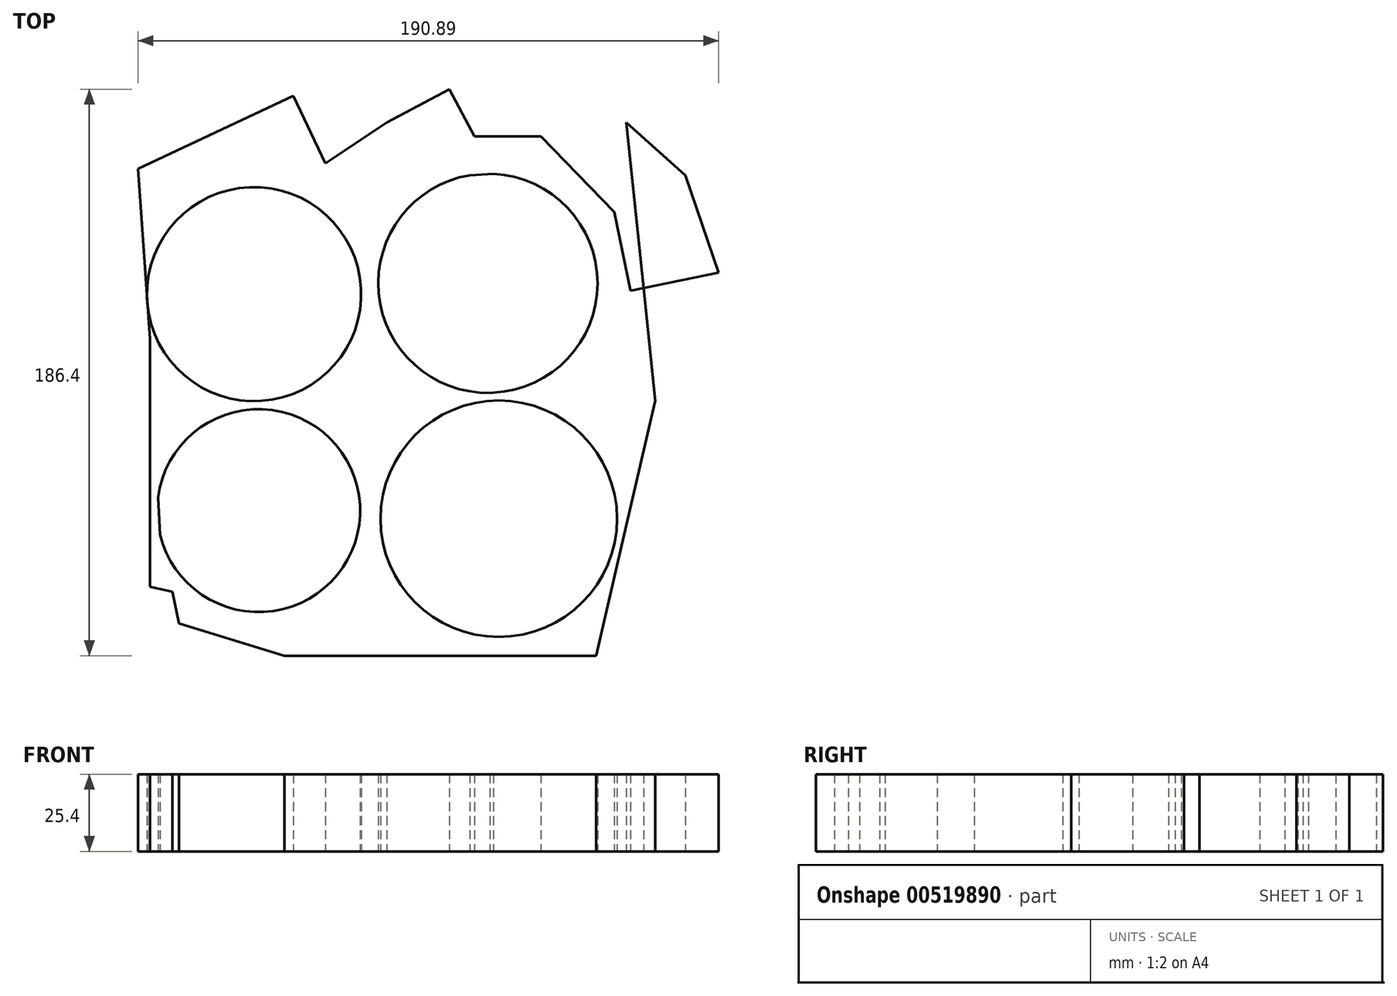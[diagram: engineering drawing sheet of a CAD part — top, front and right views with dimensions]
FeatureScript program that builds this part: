
annotation { "Feature Type Name" : "Feature", "Feature Type Description" : "" }
export const myFeature = defineFeature(function(context is Context, id is Id, definition is map)
    precondition{}
    {
        {
            var Q0;
            Q0=qCreatedBy(makeId("Top.planeOp"),FACE);
            var sketch = newSketch(context, id + "F0", { "sketchPlane" : qUnion([Q0])});
            skCircle(sketch, "E0", {"center": v(-41.12, 35.01) * mm, "radius": 35.2 * mm});
            skCircle(sketch, "E1", {"center": v(35.76, 38.59) * mm, "radius": 36.06 * mm});
            skCircle(sketch, "E2", {"center": v(-39.63, -36.2) * mm, "radius": 33.38 * mm});
            skCircle(sketch, "E3", {"center": v(39.33, -38.89) * mm, "radius": 38.9 * mm});
            skLineSegment(sketch, "E4", {"start": v(-39.94, 70.2) * mm, "end": v(37.6, 74.6) * mm});
            skLineSegment(sketch, "E5", {"start": v(37.6, 2.58) * mm, "end": v(-39.87, -0.17) * mm});
            skLineSegment(sketch, "E6", {"start": v(-39.87, -69.58) * mm, "end": v(37.6, -77.82) * mm});
            skLineSegment(sketch, "E7", {"start": v(-76.32, 34.14) * mm, "end": v(-72.07, -44.07) * mm});
            skLineSegment(sketch, "E8", {"start": v(71.81, 37.94) * mm, "end": v(77.5, -31.34) * mm});
            skSolve(sketch);
        }
        {
            var Q0;
            {var subQ0=sQuery(id+"F0.wireOp",EDGE,"E3");var subQ1=makeQuery(id+"F0.imprint","INTERSECT",VERTEX,{"derivedFrom":[subQ0,sQuery(id+"F0.wireOp",EDGE,"E8")]});Q0=makeQuery(id+"F0.imprint","IMPRINT",FACE,{"disambiguationData":[TD([[makeQuery(id+"F0.imprint","IMPRINT",EDGE,{"disambiguationData":[TD([[subQ1,-1.0]])],"derivedFrom":subQ0}),1.0]])]});}
            var Q1;
            {var subQ0=sQuery(id+"F0.wireOp",EDGE,"E2");var subQ1=makeQuery(id+"F0.imprint","INTERSECT",VERTEX,{"derivedFrom":[subQ0,sQuery(id+"F0.wireOp",EDGE,"E6")]});Q1=makeQuery(id+"F0.imprint","IMPRINT",FACE,{"disambiguationData":[TD([[makeQuery(id+"F0.imprint","IMPRINT",EDGE,{"disambiguationData":[TD([[subQ1,1.0]])],"derivedFrom":subQ0}),1.0]])]});}
            var Q2;
            {var subQ0=sQuery(id+"F0.wireOp",EDGE,"E0");var subQ1=makeQuery(id+"F0.imprint","INTERSECT",VERTEX,{"derivedFrom":[subQ0,sQuery(id+"F0.wireOp",EDGE,"E4")]});Q2=makeQuery(id+"F0.imprint","IMPRINT",FACE,{"disambiguationData":[TD([[makeQuery(id+"F0.imprint","IMPRINT",EDGE,{"disambiguationData":[TD([[subQ1,-1.0]])],"derivedFrom":subQ0}),1.0]])]});}
            var Q3;
            {var subQ0=sQuery(id+"F0.wireOp",EDGE,"E4");var subQ1=sQuery(id+"F0.wireOp",EDGE,"E1");var subQ6=makeQuery(id+"F0.imprint","INTERSECT",VERTEX,{"disambiguationData":[OD(1.0)],"derivedFrom":[subQ1,subQ0]});Q3=makeQuery(id+"F0.imprint","IMPRINT",FACE,{"disambiguationData":[TD([[makeQuery(id+"F0.imprint","IMPRINT",EDGE,{"disambiguationData":[TD([[subQ6,-1.0]])],"derivedFrom":subQ1}),1.0]])]});}
            extrude(context, id + "F1", {"entities" : qUnion([Q0, Q1, Q2, Q3]), "depth" : 25.4 * mm, "offsetDistance" : 25.4 * mm});
        }
        {
            var Q0;
            Q0=qCreatedBy(makeId("Top.planeOp"),FACE);
            var sketch = newSketch(context, id + "F2", { "sketchPlane" : qUnion([Q0])});
            skLineSegment(sketch, "E9", {"start": v(-38.18, -69.76) * mm, "end": v(-75.39, -61.26) * mm});
            skLineSegment(sketch, "E10", {"start": v(-75.39, -61.26) * mm, "end": v(-75.39, 20.25) * mm});
            skLineSegment(sketch, "E11", {"start": v(-75.39, 20.25) * mm, "end": v(-79.29, 76.24) * mm});
            skLineSegment(sketch, "E12", {"start": v(-79.29, 76.24) * mm, "end": v(-28.26, 100.33) * mm});
            skLineSegment(sketch, "E13", {"start": v(-28.26, 100.33) * mm, "end": v(-17.71, 78) * mm});
            skLineSegment(sketch, "E14", {"start": v(-17.71, 78) * mm, "end": v(2.57, 91.48) * mm});
            skLineSegment(sketch, "E15", {"start": v(2.57, 91.48) * mm, "end": v(23.13, 102.46) * mm});
            skLineSegment(sketch, "E16", {"start": v(23.13, 102.46) * mm, "end": v(31.4, 86.98) * mm});
            skLineSegment(sketch, "E17", {"start": v(31.4, 86.98) * mm, "end": v(53.25, 86.98) * mm});
            skLineSegment(sketch, "E18", {"start": v(53.25, 86.98) * mm, "end": v(77.35, 62.06) * mm});
            skLineSegment(sketch, "E19", {"start": v(77.35, 62.06) * mm, "end": v(82.66, 36.2) * mm});
            skLineSegment(sketch, "E20", {"start": v(82.66, 36.2) * mm, "end": v(111.6, 42.14) * mm});
            skLineSegment(sketch, "E21", {"start": v(111.6, 42.14) * mm, "end": v(100.73, 74.11) * mm});
            skLineSegment(sketch, "E22", {"start": v(100.73, 74.11) * mm, "end": v(81.24, 91.48) * mm});
            skLineSegment(sketch, "E23", {"start": v(81.24, 91.48) * mm, "end": v(90.81, 0) * mm});
            skLineSegment(sketch, "E24", {"start": v(90.81, 0) * mm, "end": v(81.24, -41.06) * mm});
            skLineSegment(sketch, "E25", {"start": v(81.24, -41.06) * mm, "end": v(71.32, -83.94) * mm});
            skLineSegment(sketch, "E26", {"start": v(71.32, -83.94) * mm, "end": v(-31.1, -83.94) * mm});
            skLineSegment(sketch, "E27", {"start": v(-31.1, -83.94) * mm, "end": v(-65.82, -73.3) * mm});
            skLineSegment(sketch, "E28", {"start": v(-65.82, -73.3) * mm, "end": v(-69.08, -57.45) * mm});
            skSolve(sketch);
        }
        {
            var Q0;
            Q0 = qSketchRegion(id + "F2", true);
            extrude(context, id + "F3", {"entities" : qUnion([Q0]), "depth" : 25.4 * mm, "offsetDistance" : 25.4 * mm});
        }
    });
